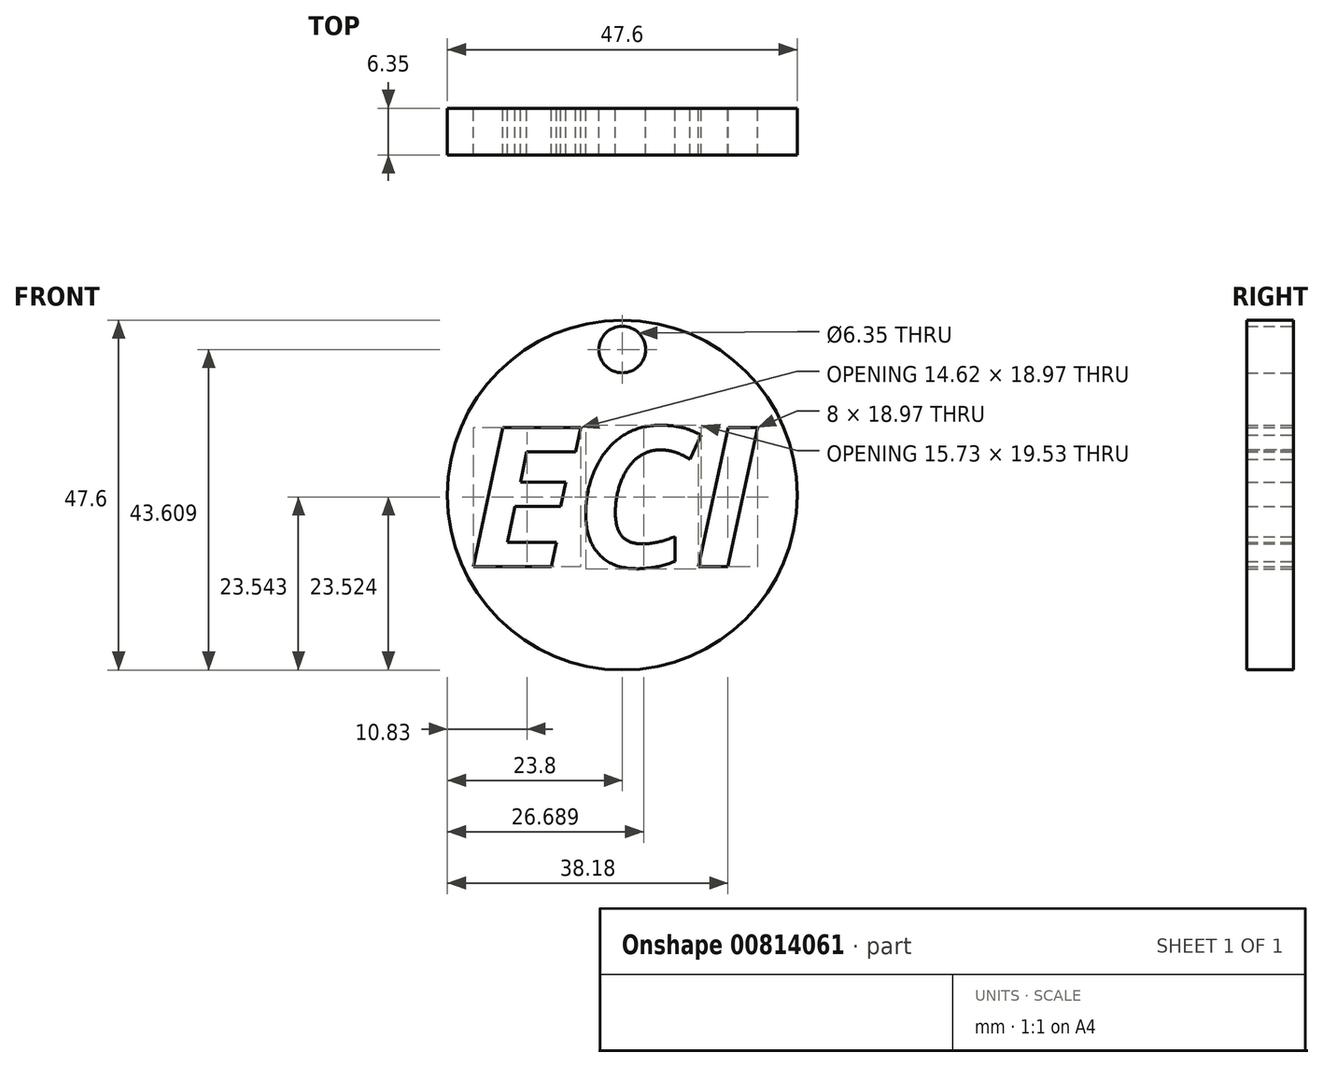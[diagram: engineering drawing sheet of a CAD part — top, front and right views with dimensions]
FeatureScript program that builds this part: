
annotation { "Feature Type Name" : "Feature", "Feature Type Description" : "" }
export const myFeature = defineFeature(function(context is Context, id is Id, definition is map)
    precondition{}
    {
        {
            var Q0;
            Q0=qCreatedBy(makeId("Front.planeOp"),FACE);
            var sketch = newSketch(context, id + "F0", { "sketchPlane" : qUnion([Q0])});
            skCircle(sketch, "E0", {"center": v(0, 0) * mm, "radius": 19 * mm});
            skText(sketch, "E1", { "text": "ECI", "fontName": "OpenSans-BoldItalic.ttf"});
            skCircle(sketch, "E2", {"center": v(0, 0) * mm, "radius": 23.8 * mm});
            const initialGuessF0  = {"E1": [-0.02097, -0.00976, 1, 0, 0.01913]};
            skSetInitialGuess(sketch, initialGuessF0);
            skSolve(sketch);
        }
        {
            var Q0;
            {var subQ1=sQuery(id+"F0.wireOp",EDGE,"E1.sketch_text.stroke-2");Q0=makeQuery(id+"F0.imprint","IMPRINT",FACE,{"disambiguationData":[TD([[makeQuery(id+"F0.imprint","IMPRINT",EDGE,{"derivedFrom":subQ1}),1.0]])]});}
            var Q1;
            Q1=makeQuery(id+"F0.imprint","IMPRINT",FACE,{"disambiguationData":[TD([[makeQuery(id+"F0.imprint","IMPRINT",EDGE,{"derivedFrom":sQuery(id+"F0.wireOp",EDGE,"E2")}),1.0]])]});
            extrude(context, id + "F1", {"entities" : qUnion([Q0, Q1]), "depth" : 6.35 * mm, "offsetDistance" : 25.4 * mm});
        }
        {
            var Q0;
            Q0=qCreatedBy(makeId("Front.planeOp"),FACE);
            var sketch = newSketch(context, id + "F2", { "sketchPlane" : qUnion([Q0])});
            skCircle(sketch, "E3", {"center": v(0, 19.8) * mm, "radius": 2.7 * mm});
            skSolve(sketch);
        }
        {
            var Q0;
            Q0=sQuery(id+"F2.wireOp",VERTEX,"E3.center");
            var Q1;
            Q1=makeQuery(id+"F1.opExtrude","SWEPT_BODY",BODY,{"disambiguationData":[OSD([sQuery(id+"F0.wireOp",EDGE,"E1.sketch_text.stroke-0"),sQuery(id+"F0.wireOp",EDGE,"E1.sketch_text.stroke-1"),sQuery(id+"F0.wireOp",EDGE,"E1.sketch_text.stroke-2"),sQuery(id+"F0.wireOp",EDGE,"E1.sketch_text.stroke-3"),sQuery(id+"F0.wireOp",EDGE,"E1.sketch_text.stroke-4"),sQuery(id+"F0.wireOp",EDGE,"E1.sketch_text.stroke-5"),sQuery(id+"F0.wireOp",EDGE,"E1.sketch_text.stroke-6"),sQuery(id+"F0.wireOp",EDGE,"E1.sketch_text.stroke-7"),sQuery(id+"F0.wireOp",EDGE,"E1.sketch_text.stroke-8"),sQuery(id+"F0.wireOp",EDGE,"E1.sketch_text.stroke-9"),sQuery(id+"F0.wireOp",EDGE,"E1.sketch_text.stroke-10"),sQuery(id+"F0.wireOp",EDGE,"E1.sketch_text.stroke-11"),sQuery(id+"F0.wireOp",EDGE,"E1.sketch_text.stroke-12"),sQuery(id+"F0.wireOp",EDGE,"E1.sketch_text.stroke-13"),sQuery(id+"F0.wireOp",EDGE,"E1.sketch_text.stroke-14"),sQuery(id+"F0.wireOp",EDGE,"E1.sketch_text.stroke-15"),sQuery(id+"F0.wireOp",EDGE,"E1.sketch_text.stroke-16"),sQuery(id+"F0.wireOp",EDGE,"E1.sketch_text.stroke-17"),sQuery(id+"F0.wireOp",EDGE,"E1.sketch_text.stroke-18"),sQuery(id+"F0.wireOp",EDGE,"E1.sketch_text.stroke-19"),sQuery(id+"F0.wireOp",EDGE,"E1.sketch_text.stroke-20"),sQuery(id+"F0.wireOp",EDGE,"E1.sketch_text.stroke-21"),sQuery(id+"F0.wireOp",EDGE,"E1.sketch_text.stroke-22"),sQuery(id+"F0.wireOp",EDGE,"E1.sketch_text.stroke-23"),sQuery(id+"F0.wireOp",EDGE,"E1.sketch_text.stroke-24"),sQuery(id+"F0.wireOp",EDGE,"E1.sketch_text.stroke-25"),sQuery(id+"F0.wireOp",EDGE,"E1.sketch_text.stroke-26"),sQuery(id+"F0.wireOp",EDGE,"E1.sketch_text.stroke-27"),sQuery(id+"F0.wireOp",EDGE,"E1.sketch_text.stroke-28"),sQuery(id+"F0.wireOp",EDGE,"E1.sketch_text.stroke-29"),sQuery(id+"F0.wireOp",EDGE,"E1.sketch_text.stroke-30"),sQuery(id+"F0.wireOp",EDGE,"E1.sketch_text.stroke-31"),sQuery(id+"F0.wireOp",EDGE,"E1.sketch_text.stroke-32"),sQuery(id+"F0.wireOp",EDGE,"E1.sketch_text.stroke-33"),sQuery(id+"F0.wireOp",EDGE,"E2")])]});
            hole(context, id + "F3", {"style" : HoleStyle.SIMPLE, "endStyle" : HoleEndStyle.THROUGH, "oppositeDirection" : true, "holeDiameter" : 6.35 * mm, "majorDiameter" : 6.35 * mm, "isTappedThrough" : true, "tappedDepth" : 12.7 * mm, "tapClearance" : 3, "locations" : qUnion([Q0]), "scope" : qUnion([Q1])});
        }
    });
